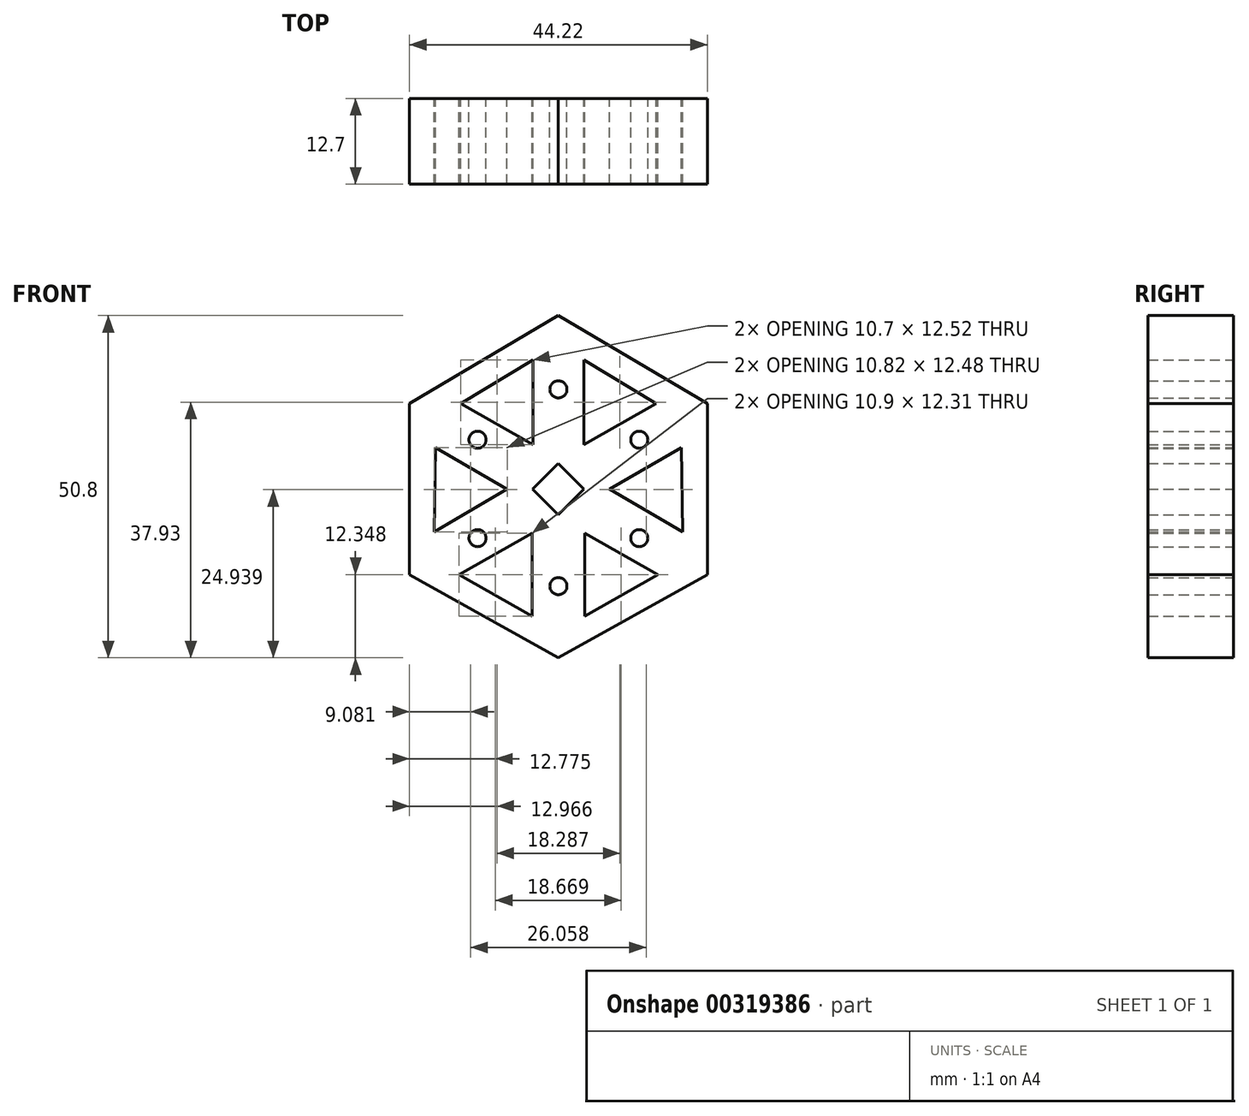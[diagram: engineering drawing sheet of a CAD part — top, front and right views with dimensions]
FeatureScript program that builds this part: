
annotation { "Feature Type Name" : "Feature", "Feature Type Description" : "" }
export const myFeature = defineFeature(function(context is Context, id is Id, definition is map)
    precondition{}
    {
        {
            var Q0;
            Q0=qCreatedBy(makeId("Front.planeOp"),FACE);
            var sketch = newSketch(context, id + "F0", { "sketchPlane" : qUnion([Q0])});
            skLineSegment(sketch, "E0", {"start": v(-22.11, 12.7) * mm, "end": v(-22.11, -12.7) * mm});
            skLineSegment(sketch, "E1", {"start": v(0, -25.06) * mm, "end": v(-22.11, -12.7) * mm});
            skLineSegment(sketch, "E2", {"start": v(-22.11, 12.7) * mm, "end": v(0, 25.74) * mm});
            skLineSegment(sketch, "E3.MirrorCS", {"start": v(22.11, 12.7) * mm, "end": v(0, 25.74) * mm});
            skLineSegment(sketch, "E4.MirrorCS", {"start": v(22.11, 12.7) * mm, "end": v(22.11, -12.7) * mm});
            skLineSegment(sketch, "E5.MirrorCS", {"start": v(0, -25.06) * mm, "end": v(22.11, -12.7) * mm});
            skLineSegment(sketch, "E6", {"start": v(3.8, 19.13) * mm, "end": v(3.8, 6.6) * mm});
            skLineSegment(sketch, "E7", {"start": v(3.8, 6.6) * mm, "end": v(14.5, 12.7) * mm});
            skLineSegment(sketch, "E8", {"start": v(14.5, 12.7) * mm, "end": v(3.8, 19.13) * mm});
            skLineSegment(sketch, "E9.MirrorCS", {"start": v(-3.8, 19.13) * mm, "end": v(-3.8, 6.6) * mm});
            skLineSegment(sketch, "E10.MirrorCS", {"start": v(-14.5, 12.7) * mm, "end": v(-3.8, 19.13) * mm});
            skLineSegment(sketch, "E11.MirrorCS", {"start": v(-3.8, 6.6) * mm, "end": v(-14.5, 12.7) * mm});
            skLineSegment(sketch, "E12.MirrorCS", {"start": v(18.44, -6.36) * mm, "end": v(7.62, -0.05) * mm});
            skLineSegment(sketch, "E13.MirrorCS", {"start": v(18.27, 6.12) * mm, "end": v(18.44, -6.36) * mm});
            skLineSegment(sketch, "E14.MirrorCS", {"start": v(7.62, -0.05) * mm, "end": v(18.27, 6.12) * mm});
            skLineSegment(sketch, "E15.MirrorCS", {"start": v(-7.62, -0.05) * mm, "end": v(-18.27, 6.12) * mm});
            skLineSegment(sketch, "E16.MirrorCS", {"start": v(-18.27, 6.12) * mm, "end": v(-18.44, -6.36) * mm});
            skLineSegment(sketch, "E17.MirrorCS", {"start": v(-18.44, -6.36) * mm, "end": v(-7.62, -0.05) * mm});
            skLineSegment(sketch, "E18.MirrorCS", {"start": v(-3.92, -18.87) * mm, "end": v(-14.79, -12.72) * mm});
            skLineSegment(sketch, "E19.MirrorCS", {"start": v(-3.88, -6.56) * mm, "end": v(-3.92, -18.87) * mm});
            skLineSegment(sketch, "E20.MirrorCS", {"start": v(-14.79, -12.72) * mm, "end": v(-3.88, -6.56) * mm});
            skLineSegment(sketch, "E21.MirrorCS", {"start": v(14.79, -12.72) * mm, "end": v(3.88, -6.56) * mm});
            skLineSegment(sketch, "E22.MirrorCS", {"start": v(3.92, -18.87) * mm, "end": v(14.79, -12.72) * mm});
            skLineSegment(sketch, "E23.MirrorCS", {"start": v(3.88, -6.56) * mm, "end": v(3.92, -18.87) * mm});
            skLineSegment(sketch, "E24", {"start": v(0, 3.81) * mm, "end": v(-3.81, 0) * mm});
            skLineSegment(sketch, "E25", {"start": v(0, -3.81) * mm, "end": v(-3.81, 0) * mm});
            skLineSegment(sketch, "E26", {"start": v(0, -3.81) * mm, "end": v(3.81, 0) * mm});
            skLineSegment(sketch, "E27", {"start": v(3.81, 0) * mm, "end": v(0, 3.81) * mm});
            skCircle(sketch, "E28", {"center": v(-12, 7.3) * mm, "radius": 1.27 * mm});
            skCircle(sketch, "E29", {"center": v(0, 14.77) * mm, "radius": 1.27 * mm});
            skCircle(sketch, "E30", {"center": v(12, 7.3) * mm, "radius": 1.27 * mm});
            skCircle(sketch, "E31", {"center": v(12, -7.3) * mm, "radius": 1.27 * mm});
            skCircle(sketch, "E32", {"center": v(0, -14.44) * mm, "radius": 1.27 * mm});
            skCircle(sketch, "E33", {"center": v(-12, -7.3) * mm, "radius": 1.27 * mm});
            skSolve(sketch);
        }
        {
            var Q0;
            Q0=makeQuery(id+"F0.imprint","IMPRINT",FACE,{"disambiguationData":[TD([[makeQuery(id+"F0.imprint","IMPRINT",EDGE,{"derivedFrom":sQuery(id+"F0.wireOp",EDGE,"E0")}),1.0]])]});
            extrude(context, id + "F1", {"entities" : qUnion([Q0]), "depth" : 12.7 * mm, "offsetDistance" : 25.4 * mm});
        }
    });
